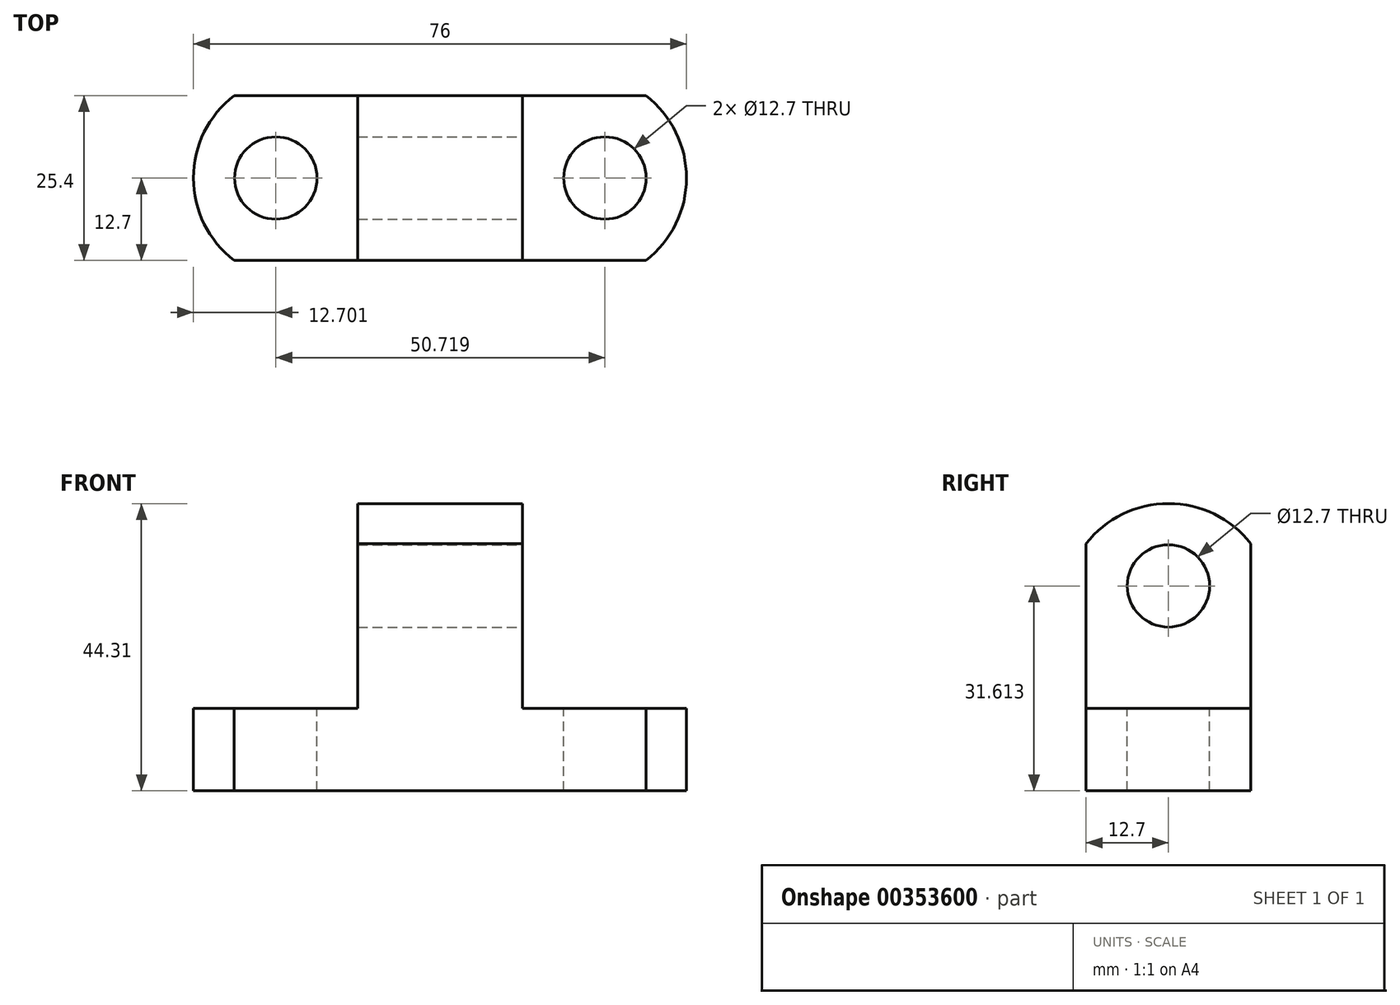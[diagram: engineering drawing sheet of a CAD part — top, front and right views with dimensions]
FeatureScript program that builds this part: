
annotation { "Feature Type Name" : "Feature", "Feature Type Description" : "" }
export const myFeature = defineFeature(function(context is Context, id is Id, definition is map)
    precondition{}
    {
        {
            var Q0;
            Q0=qCreatedBy(makeId("Top.planeOp"),FACE);
            var sketch = newSketch(context, id + "F0", { "sketchPlane" : qUnion([Q0])});
            skLineSegment(sketch, "E0.bottom", {"start": v(0, 0) * mm, "end": v(76.2, 0) * mm});
            skLineSegment(sketch, "E0.top", {"start": v(0, 25.4) * mm, "end": v(76.2, 25.4) * mm});
            skLineSegment(sketch, "E0.left", {"start": v(0, 0) * mm, "end": v(0, 25.4) * mm});
            skLineSegment(sketch, "E0.right", {"start": v(76.2, 0) * mm, "end": v(76.2, 25.4) * mm});
            skSolve(sketch);
        }
        {
            var Q0;
            Q0=makeQuery(id+"F0.imprint","IMPRINT",FACE,{"disambiguationData":[TD([[makeQuery(id+"F0.imprint","IMPRINT",EDGE,{"derivedFrom":sQuery(id+"F0.wireOp",EDGE,"E0.bottom")}),1.0]])]});
            extrude(context, id + "F1", {"entities" : qUnion([Q0]), "depth" : 12.7 * mm});
        }
        {
            var Q0;
            Q0=makeQuery(id+"F1.opExtrude","CAP_FACE",FACE,{"disambiguationData":[OSD([sQuery(id+"F0.wireOp",EDGE,"E0.bottom"),sQuery(id+"F0.wireOp",EDGE,"E0.top"),sQuery(id+"F0.wireOp",EDGE,"E0.left"),sQuery(id+"F0.wireOp",EDGE,"E0.right")])],"isStart":false});
            var sketch = newSketch(context, id + "F2", { "sketchPlane" : qUnion([Q0])});
            skArc(sketch, "E1", {"start": v(6.35, 25.4) * mm, "mid": v(0.08, 12.7) * mm, "end": v(6.35, 0) * mm});
            skLineSegment(sketch, "E2", {"start": v(6.35, 25.4) * mm, "end": v(0, 25.4) * mm});
            skLineSegment(sketch, "E3", {"start": v(0, 25.4) * mm, "end": v(0, 0) * mm});
            skLineSegment(sketch, "E4", {"start": v(0, 0) * mm, "end": v(6.35, 0) * mm});
            skLineSegment(sketch, "E5", {"start": v(76.2, 25.4) * mm, "end": v(69.85, 25.4) * mm});
            skLineSegment(sketch, "E6", {"start": v(76.2, 25.4) * mm, "end": v(76.2, 0) * mm});
            skLineSegment(sketch, "E7", {"start": v(76.2, 0) * mm, "end": v(69.85, 0) * mm});
            skArc(sketch, "E8", {"start": v(69.85, 0) * mm, "mid": v(76.08, 12.7) * mm, "end": v(69.85, 25.4) * mm});
            skSolve(sketch);
        }
        {
            var Q0;
            Q0=makeQuery(id+"F2.imprint","IMPRINT",FACE,{"disambiguationData":[TD([[makeQuery(id+"F2.imprint","IMPRINT",EDGE,{"derivedFrom":sQuery(id+"F2.wireOp",EDGE,"E1")}),-1.0]])]});
            var Q1;
            Q1=makeQuery(id+"F2.imprint","IMPRINT",FACE,{"disambiguationData":[TD([[makeQuery(id+"F2.imprint","IMPRINT",EDGE,{"derivedFrom":sQuery(id+"F2.wireOp",EDGE,"E5")}),-1.0]])]});
            extrude(context, id + "F3", {"entities" : qUnion([Q0, Q1]), "operationType" : NewBodyOperationType.REMOVE, "oppositeDirection" : true, "depth" : 25.4 * mm});
        }
        {
            var Q0;
            Q0=makeQuery(id+"F1.opExtrude","CAP_FACE",FACE,{"disambiguationData":[OSD([sQuery(id+"F0.wireOp",EDGE,"E0.bottom"),sQuery(id+"F0.wireOp",EDGE,"E0.top"),sQuery(id+"F0.wireOp",EDGE,"E0.left"),sQuery(id+"F0.wireOp",EDGE,"E0.right")])],"isStart":false});
            var sketch = newSketch(context, id + "F4", { "sketchPlane" : qUnion([Q0])});
            skLineSegment(sketch, "E9", {"start": v(25.4, 25.4) * mm, "end": v(25.4, 0) * mm});
            skLineSegment(sketch, "E10", {"start": v(25.4, 0) * mm, "end": v(50.8, 0) * mm});
            skLineSegment(sketch, "E11", {"start": v(50.8, 0) * mm, "end": v(50.8, 25.4) * mm});
            skLineSegment(sketch, "E12", {"start": v(50.8, 25.4) * mm, "end": v(25.4, 25.4) * mm});
            skSolve(sketch);
        }
        {
            var Q0;
            Q0=makeQuery(id+"F4.imprint","IMPRINT",FACE,{"disambiguationData":[TD([[makeQuery(id+"F4.imprint","IMPRINT",EDGE,{"derivedFrom":sQuery(id+"F4.wireOp",EDGE,"E9")}),1.0]])]});
            extrude(context, id + "F5", {"entities" : qUnion([Q0]), "operationType" : NewBodyOperationType.ADD, "depth" : 31.75 * mm});
        }
        {
            var Q0;
            Q0=makeQuery(id+"F5.opExtrude","SWEPT_FACE",FACE,{"disambiguationData":[OSD([sQuery(id+"F4.wireOp",EDGE,"E11")])]});
            var sketch = newSketch(context, id + "F6", { "sketchPlane" : qUnion([Q0])});
            skLineSegment(sketch, "E13", {"start": v(0, 38.1) * mm, "end": v(0, 44.45) * mm});
            skLineSegment(sketch, "E14", {"start": v(0, 44.45) * mm, "end": v(25.4, 44.45) * mm});
            skLineSegment(sketch, "E15", {"start": v(25.4, 44.45) * mm, "end": v(25.4, 38.1) * mm});
            skArc(sketch, "E16", {"start": v(25.4, 38.1) * mm, "mid": v(12.7, 44.31) * mm, "end": v(0, 38.1) * mm});
            skSolve(sketch);
        }
        {
            var Q0;
            Q0=makeQuery(id+"F6.imprint","IMPRINT",FACE,{"disambiguationData":[TD([[makeQuery(id+"F6.imprint","IMPRINT",EDGE,{"derivedFrom":sQuery(id+"F6.wireOp",EDGE,"E13")}),1.0]])]});
            extrude(context, id + "F7", {"entities" : qUnion([Q0]), "operationType" : NewBodyOperationType.REMOVE, "oppositeDirection" : true, "depth" : 25.4 * mm});
        }
        {
            var Q0;
            {var subQ0=sQuery(id+"F0.wireOp",EDGE,"E0.top");var subQ1=sQuery(id+"F0.wireOp",EDGE,"E0.bottom");Q0=makeQuery(id+"F5.boolean.opBoolean","SPLIT",FACE,{"disambiguationData":[TD([makeQuery(id+"F3.boolean.opBoolean","COPY",FACE,{"derivedFrom":makeQuery(id+"F3.opExtrude","SWEPT_FACE",FACE,{"disambiguationData":[OSD([sQuery(id+"F2.wireOp",EDGE,"E1")])]})})])],"derivedFrom":makeQuery(id+"F1.opExtrude","CAP_FACE",FACE,{"disambiguationData":[OSD([subQ1,subQ0,sQuery(id+"F0.wireOp",EDGE,"E0.left"),sQuery(id+"F0.wireOp",EDGE,"E0.right")])],"isStart":false})});}
            var sketch = newSketch(context, id + "F8", { "sketchPlane" : qUnion([Q0])});
            skCircle(sketch, "E17", {"center": v(12.78, 12.7) * mm, "radius": 6.35 * mm});
            skPoint(sketch, "E17.centerSnap0", {"position": v(25.4, 12.7) * mm});
            skCircle(sketch, "E18", {"center": v(63.5, 12.7) * mm, "radius": 6.35 * mm});
            skSolve(sketch);
        }
        {
            var Q0;
            Q0=makeQuery(id+"F8.imprint","IMPRINT",FACE,{"disambiguationData":[TD([[makeQuery(id+"F8.imprint","IMPRINT",EDGE,{"derivedFrom":sQuery(id+"F8.wireOp",EDGE,"E17")}),1.0]])]});
            var Q1;
            Q1=makeQuery(id+"F8.imprint","IMPRINT",FACE,{"disambiguationData":[TD([[makeQuery(id+"F8.imprint","IMPRINT",EDGE,{"derivedFrom":sQuery(id+"F8.wireOp",EDGE,"E18")}),1.0]])]});
            extrude(context, id + "F9", {"entities" : qUnion([Q0, Q1]), "operationType" : NewBodyOperationType.REMOVE, "oppositeDirection" : true, "depth" : 12.7 * mm});
        }
        {
            var Q0;
            Q0=makeQuery(id+"F5.opExtrude","SWEPT_FACE",FACE,{"disambiguationData":[OSD([sQuery(id+"F4.wireOp",EDGE,"E11")])]});
            var sketch = newSketch(context, id + "F10", { "sketchPlane" : qUnion([Q0])});
            skCircle(sketch, "E19", {"center": v(12.7, 31.61) * mm, "radius": 6.35 * mm});
            skSolve(sketch);
        }
        {
            var Q0;
            Q0=makeQuery(id+"F10.imprint","IMPRINT",FACE,{"disambiguationData":[TD([[makeQuery(id+"F10.imprint","IMPRINT",EDGE,{"derivedFrom":sQuery(id+"F10.wireOp",EDGE,"E19")}),1.0]])]});
            extrude(context, id + "F11", {"entities" : qUnion([Q0]), "operationType" : NewBodyOperationType.REMOVE, "oppositeDirection" : true, "depth" : 25.4 * mm});
        }
    });
